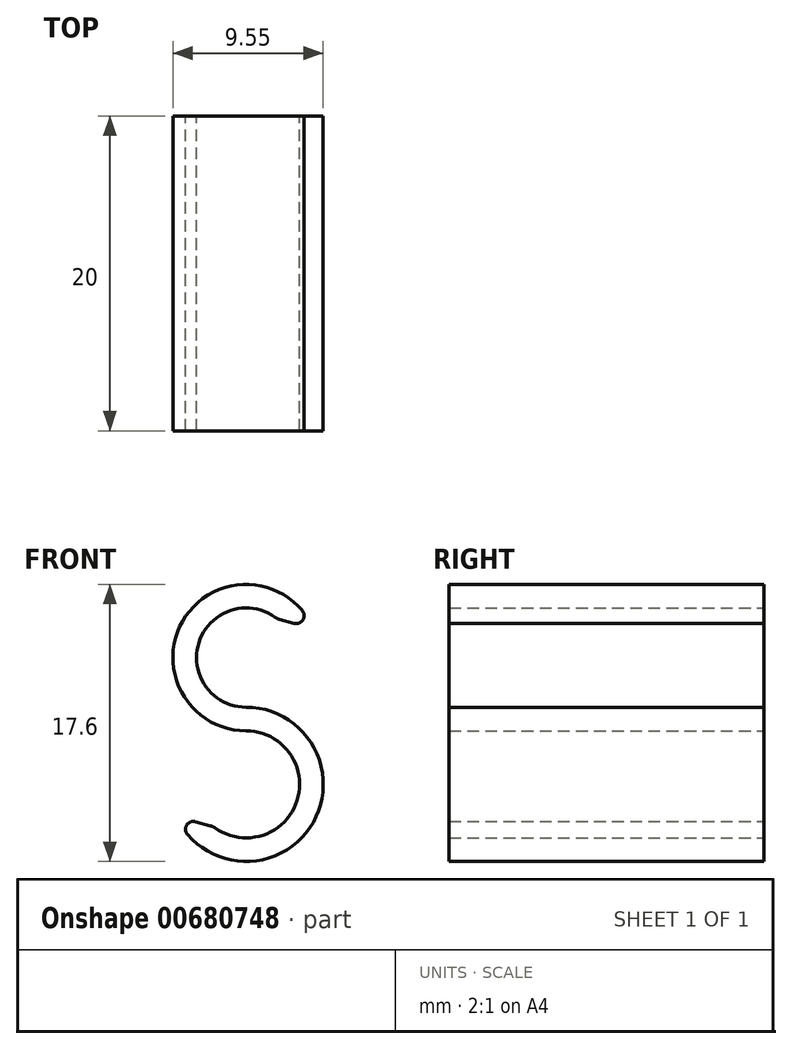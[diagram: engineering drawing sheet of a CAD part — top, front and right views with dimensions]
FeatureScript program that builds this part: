
annotation { "Feature Type Name" : "Feature", "Feature Type Description" : "" }
export const myFeature = defineFeature(function(context is Context, id is Id, definition is map)
    precondition{}
    {
        {
            var Q0;
            Q0=qCreatedBy(makeId("Front.planeOp"),FACE);
            var sketch = newSketch(context, id + "F0", { "sketchPlane" : qUnion([Q0])});
            skArc(sketch, "E0", {"start": v(-1.97, -2.77) * mm, "mid": v(3.24, -1.03) * mm, "end": v(0, 3.4) * mm});
            skArc(sketch, "E1", {"start": v(1.82, 10.62) * mm, "mid": v(-3, 9) * mm, "end": v(0, 4.9) * mm});
            skArc(sketch, "E2.0", {"start": v(3.57, 11.03) * mm, "mid": v(-4.21, 10.02) * mm, "end": v(0, 3.4) * mm});
            skArc(sketch, "E3.0", {"start": v(-3.73, -3.18) * mm, "mid": v(4.45, -2.05) * mm, "end": v(0, 4.9) * mm});
            skLineSegment(sketch, "E4", {"start": v(2.14, 10.47) * mm, "end": v(3.06, 10.23) * mm});
            skLineSegment(sketch, "E5", {"start": v(-2.29, -2.62) * mm, "end": v(-3.22, -2.37) * mm});
            skLineSegment(sketch, "E6", {"start": v(0, 0) * mm, "end": v(-7.33, 1.97) * mm, "construction": true});
            skLineSegment(sketch, "E7", {"start": v(0, 0) * mm, "end": v(-7.6, 0) * mm, "construction": true});
            skLineSegment(sketch, "E8", {"start": v(0, 8.05) * mm, "end": v(7.6, 8.05) * mm, "construction": true});
            skLineSegment(sketch, "E9", {"start": v(0, 8.05) * mm, "end": v(7.33, 6.08) * mm, "construction": true});
            skPoint(sketch, "E10.visualSharp", {"position": v(1.95, 10.52) * mm});
            skArc(sketch, "E10.filletArc", {"start": v(1.82, 10.62) * mm, "mid": v(1.97, 10.53) * mm, "end": v(2.14, 10.47) * mm});
            skPoint(sketch, "E11.visualSharp", {"position": v(4.26, 9.9) * mm});
            skArc(sketch, "E11.filletArc", {"start": v(3.06, 10.23) * mm, "mid": v(3.6, 10.44) * mm, "end": v(3.57, 11.03) * mm});
            skPoint(sketch, "E12.visualSharp", {"position": v(-2.1, -2.67) * mm});
            skArc(sketch, "E12.filletArc", {"start": v(-1.97, -2.77) * mm, "mid": v(-2.12, -2.68) * mm, "end": v(-2.29, -2.62) * mm});
            skPoint(sketch, "E13.visualSharp", {"position": v(-4.45, -2.04) * mm});
            skArc(sketch, "E13.filletArc", {"start": v(-3.22, -2.37) * mm, "mid": v(-3.77, -2.6) * mm, "end": v(-3.73, -3.18) * mm});
            skCircle(sketch, "E14", {"center": v(2.53, 7.37) * mm, "radius": 2.9 * mm, "construction": true});
            skCircle(sketch, "E15", {"center": v(-2.08, 0.56) * mm, "radius": 3.13 * mm, "construction": true});
            skSolve(sketch);
        }
        {
            var Q0;
            Q0 = qSketchRegion(id + "F0", true);
            extrude(context, id + "F1", {"entities" : qUnion([Q0]), "depth" : 20 * mm, "offsetDistance" : 25 * mm});
        }
    });
